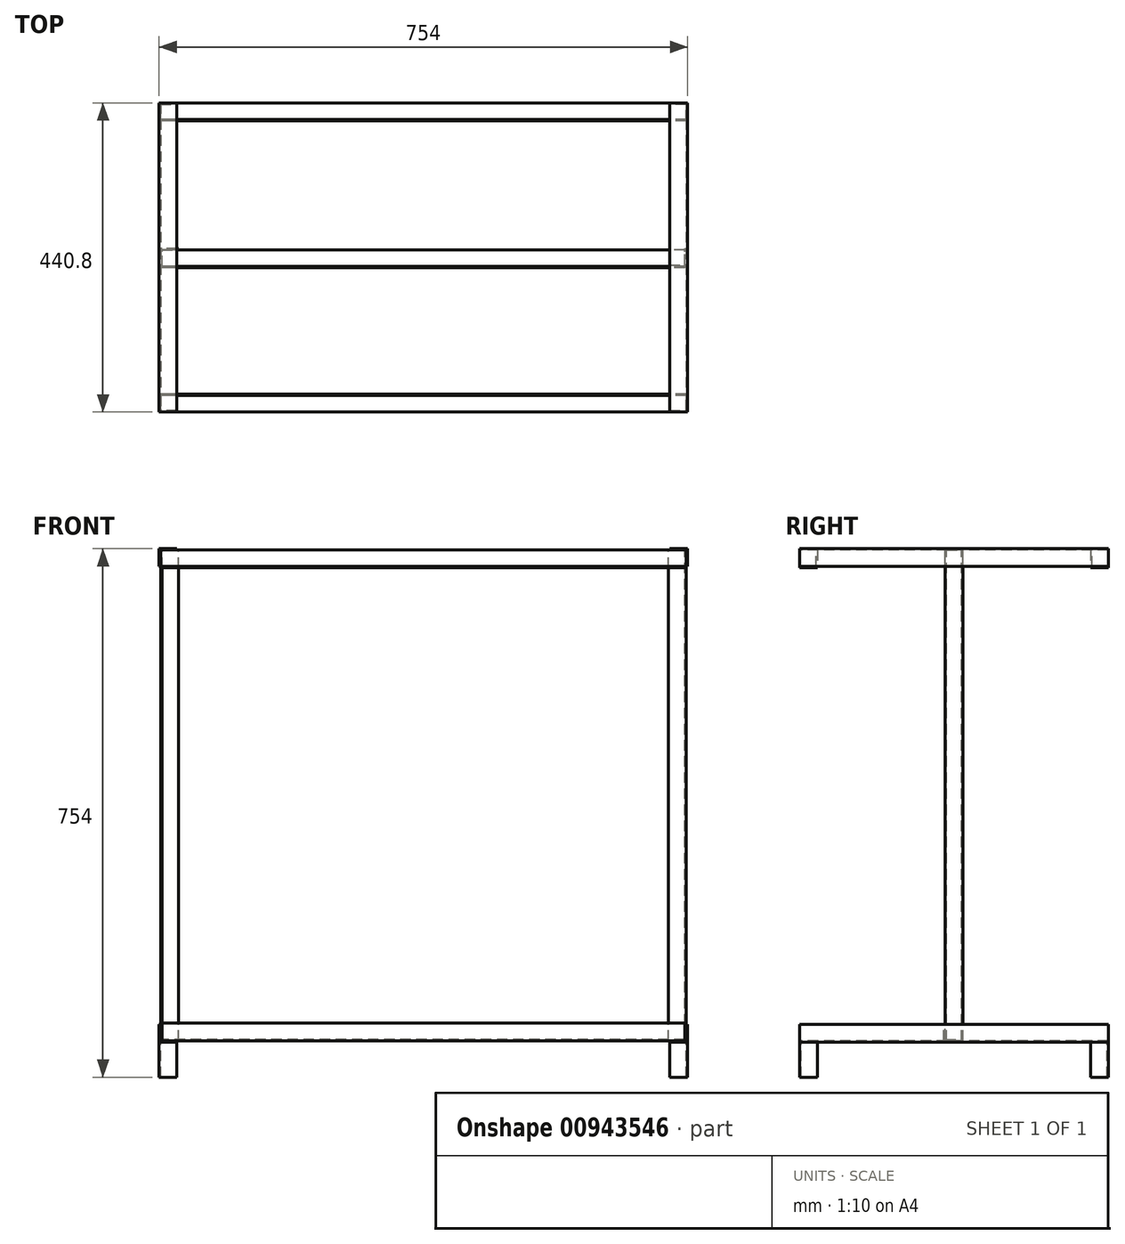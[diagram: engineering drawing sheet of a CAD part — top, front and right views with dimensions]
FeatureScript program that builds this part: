
annotation { "Feature Type Name" : "Feature", "Feature Type Description" : "" }
export const myFeature = defineFeature(function(context is Context, id is Id, definition is map)
    precondition{}
    {
        {
            var Q0;
            Q0=qCreatedBy(makeId("Front.planeOp"),FACE);
            var sketch = newSketch(context, id + "F0", { "sketchPlane" : qUnion([Q0])});
            skLineSegment(sketch, "E0.bottom", {"start": v(0, 0) * mm, "end": v(2, 0) * mm});
            skLineSegment(sketch, "E0.top", {"start": v(0, 25.4) * mm, "end": v(25.4, 25.4) * mm});
            skLineSegment(sketch, "E0.left", {"start": v(0, 0) * mm, "end": v(0, 25.4) * mm});
            skLineSegment(sketch, "E0.right", {"start": v(25.4, 23.4) * mm, "end": v(25.4, 25.4) * mm});
            skLineSegment(sketch, "E1.top", {"start": v(25.4, 23.4) * mm, "end": v(2, 23.4) * mm});
            skLineSegment(sketch, "E1.right", {"start": v(2, 0) * mm, "end": v(2, 23.4) * mm});
            skSolve(sketch);
        }
        {
            var Q0;
            Q0 = qSketchRegion(id + "F0", true);
            extrude(context, id + "F1", {"entities" : qUnion([Q0]), "oppositeDirection" : true, "depth" : 440.8 * mm, "offsetDistance" : 25 * mm});
        }
        {
            var Q0;
            Q0=makeQuery(id+"F1.opExtrude","SWEPT_FACE",FACE,{"disambiguationData":[OSD([sQuery(id+"F0.wireOp",EDGE,"E1.right")])]});
            var sketch = newSketch(context, id + "F2", { "sketchPlane" : qUnion([Q0])});
            skLineSegment(sketch, "E2", {"start": v(25.4, 23.4) * mm, "end": v(25.4, -2) * mm});
            skLineSegment(sketch, "E3", {"start": v(25.4, -2) * mm, "end": v(0, -2) * mm});
            skLineSegment(sketch, "E4", {"start": v(0, -2) * mm, "end": v(0, 0) * mm});
            skLineSegment(sketch, "E5", {"start": v(0, 0) * mm, "end": v(23.4, 0) * mm});
            skLineSegment(sketch, "E6", {"start": v(23.4, 0) * mm, "end": v(23.4, 23.4) * mm});
            skLineSegment(sketch, "E7", {"start": v(23.4, 23.4) * mm, "end": v(25.4, 23.4) * mm});
            skLineSegment(sketch, "E8", {"start": v(220.4, 23.4) * mm, "end": v(220.4, 0) * mm, "construction": true});
            skLineSegment(sketch, "E9.MirrorCS", {"start": v(417.4, 23.4) * mm, "end": v(415.4, 23.4) * mm});
            skLineSegment(sketch, "E10.MirrorCS", {"start": v(440.8, -2) * mm, "end": v(440.8, 0) * mm});
            skLineSegment(sketch, "E11.MirrorCS", {"start": v(415.4, 23.4) * mm, "end": v(415.4, -2) * mm});
            skLineSegment(sketch, "E12.MirrorCS", {"start": v(415.4, -2) * mm, "end": v(440.8, -2) * mm});
            skLineSegment(sketch, "E13.MirrorCS", {"start": v(440.8, 0) * mm, "end": v(417.4, 0) * mm});
            skLineSegment(sketch, "E14.MirrorCS", {"start": v(417.4, 0) * mm, "end": v(417.4, 23.4) * mm});
            skSolve(sketch);
        }
        {
            var Q0;
            {var subQ5=sQuery(id+"F2.wireOp",EDGE,"E6");Q0=makeQuery(id+"F2.imprint","IMPRINT",FACE,{"disambiguationData":[TD([[makeQuery(id+"F2.imprint","IMPRINT",EDGE,{"derivedFrom":subQ5}),-1.0]])]});}
            var Q1;
            {var subQ1=sQuery(id+"F2.wireOp",EDGE,"E3");Q1=makeQuery(id+"F2.imprint","IMPRINT",FACE,{"disambiguationData":[TD([[makeQuery(id+"F2.imprint","IMPRINT",EDGE,{"derivedFrom":subQ1}),-1.0]])]});}
            var Q2;
            {var subQ0=sQuery(id+"F2.wireOp",EDGE,"E9.MirrorCS");Q2=makeQuery(id+"F2.imprint","IMPRINT",FACE,{"disambiguationData":[TD([[makeQuery(id+"F2.imprint","IMPRINT",EDGE,{"derivedFrom":subQ0}),1.0]])]});}
            var Q3;
            Q3=makeQuery(id+"F2.imprint","IMPRINT",FACE,{"disambiguationData":[TD([[makeQuery(id+"F2.imprint","IMPRINT",EDGE,{"derivedFrom":sQuery(id+"F2.wireOp",EDGE,"E10.MirrorCS")}),1.0]])]});
            extrude(context, id + "F3", {"entities" : qUnion([Q0, Q1, Q2, Q3]), "depth" : 750 * mm, "offsetDistance" : 25 * mm});
        }
        {
            var Q0;
            Q0=qCreatedBy(makeId("Front.planeOp"),FACE);
            var sketch = newSketch(context, id + "F4", { "sketchPlane" : qUnion([Q0])});
            skLineSegment(sketch, "E15.0", {"start": v(752, 23.4) * mm, "end": v(2, 23.4) * mm, "construction": true});
            skLineSegment(sketch, "E15.1", {"start": v(752, -2) * mm, "end": v(2, -2) * mm, "construction": true});
            skLineSegment(sketch, "E16", {"start": v(377, 23.4) * mm, "end": v(377, -2) * mm, "construction": true});
            skLineSegment(sketch, "E17.0", {"start": v(0, 0) * mm, "end": v(0, 25.4) * mm});
            skLineSegment(sketch, "E17.1", {"start": v(0, 0) * mm, "end": v(2, 0) * mm});
            skLineSegment(sketch, "E17.2", {"start": v(2, 0) * mm, "end": v(2, 23.4) * mm});
            skLineSegment(sketch, "E17.3", {"start": v(0, 25.4) * mm, "end": v(25.4, 25.4) * mm});
            skLineSegment(sketch, "E17.4", {"start": v(25.4, 23.4) * mm, "end": v(25.4, 25.4) * mm});
            skLineSegment(sketch, "E18.MirrorCS", {"start": v(754, 0) * mm, "end": v(752, 0) * mm});
            skLineSegment(sketch, "E19.MirrorCS", {"start": v(728.6, 23.4) * mm, "end": v(728.6, 25.4) * mm});
            skLineSegment(sketch, "E20.MirrorCS", {"start": v(754, 0) * mm, "end": v(754, 25.4) * mm});
            skLineSegment(sketch, "E21.MirrorCS", {"start": v(754, 25.4) * mm, "end": v(728.6, 25.4) * mm});
            skLineSegment(sketch, "E22.MirrorCS", {"start": v(752, 0) * mm, "end": v(752, 23.4) * mm});
            skLineSegment(sketch, "E23", {"start": v(728.6, 23.4) * mm, "end": v(752, 23.4) * mm});
            skSolve(sketch);
        }
        {
            var Q0;
            Q0 = qSketchRegion(id + "F4", true);
            extrude(context, id + "F5", {"entities" : qUnion([Q0]), "oppositeDirection" : true, "depth" : 440.8 * mm, "offsetDistance" : 25 * mm});
        }
        {
            var Q0;
            Q0=makeQuery(id+"F1.opExtrude","SWEPT_FACE",FACE,{"disambiguationData":[OSD([sQuery(id+"F0.wireOp",EDGE,"E1.top")])]});
            var sketch = newSketch(context, id + "F6", { "sketchPlane" : qUnion([Q0])});
            skLineSegment(sketch, "E24.0", {"start": v(0, -440.8) * mm, "end": v(0, 0) * mm, "construction": true});
            skLineSegment(sketch, "E24.1", {"start": v(754, -440.8) * mm, "end": v(754, 0) * mm, "construction": true});
            skLineSegment(sketch, "E25", {"start": v(0, -220.4) * mm, "end": v(754, -220.4) * mm, "construction": true});
            skLineSegment(sketch, "E26", {"start": v(2, -220.4) * mm, "end": v(2, -207.7) * mm});
            skLineSegment(sketch, "E27", {"start": v(2, -207.7) * mm, "end": v(4, -207.7) * mm});
            skLineSegment(sketch, "E28", {"start": v(4, -207.7) * mm, "end": v(4, -231.1) * mm});
            skLineSegment(sketch, "E29", {"start": v(4, -231.1) * mm, "end": v(27.4, -231.1) * mm});
            skLineSegment(sketch, "E30", {"start": v(27.4, -231.1) * mm, "end": v(27.4, -233.1) * mm});
            skLineSegment(sketch, "E31", {"start": v(27.4, -233.1) * mm, "end": v(2, -233.1) * mm});
            skLineSegment(sketch, "E32", {"start": v(2, -233.1) * mm, "end": v(2, -220.4) * mm});
            skLineSegment(sketch, "E33", {"start": v(752, -220.4) * mm, "end": v(752, -207.7) * mm});
            skLineSegment(sketch, "E34", {"start": v(752, -207.7) * mm, "end": v(726.6, -207.7) * mm});
            skLineSegment(sketch, "E35", {"start": v(726.6, -207.7) * mm, "end": v(726.6, -209.7) * mm});
            skLineSegment(sketch, "E36", {"start": v(726.6, -209.7) * mm, "end": v(750, -209.7) * mm});
            skLineSegment(sketch, "E37", {"start": v(750, -209.7) * mm, "end": v(750, -233.1) * mm});
            skLineSegment(sketch, "E38", {"start": v(750, -233.1) * mm, "end": v(752, -233.1) * mm});
            skLineSegment(sketch, "E39", {"start": v(752, -233.1) * mm, "end": v(752, -220.4) * mm});
            skSolve(sketch);
        }
        {
            var Q0;
            Q0 = qSketchRegion(id + "F6", true);
            extrude(context, id + "F7", {"entities" : qUnion([Q0]), "depth" : 700 * mm, "offsetDistance" : 25 * mm});
        }
        {
            var Q0;
            Q0=qCreatedBy(makeId("Front.planeOp"),FACE);
            var sketch = newSketch(context, id + "F8", { "sketchPlane" : qUnion([Q0])});
            skLineSegment(sketch, "E40.0", {"start": v(27.4, -676.6) * mm, "end": v(27.4, 23.4) * mm, "construction": true});
            skLineSegment(sketch, "E40.1", {"start": v(726.6, -676.6) * mm, "end": v(726.6, 23.4) * mm, "construction": true});
            skLineSegment(sketch, "E41", {"start": v(27.4, -326.6) * mm, "end": v(726.6, -326.6) * mm, "construction": true});
            skLineSegment(sketch, "E42.0", {"start": v(0, 25.4) * mm, "end": v(25.4, 25.4) * mm, "construction": true});
            skLineSegment(sketch, "E42.1", {"start": v(2, 0) * mm, "end": v(2, 23.4) * mm, "construction": true});
            skLineSegment(sketch, "E42.2", {"start": v(25.4, 23.4) * mm, "end": v(2, 23.4) * mm, "construction": true});
            skLineSegment(sketch, "E42.3", {"start": v(25.4, 23.4) * mm, "end": v(25.4, 25.4) * mm, "construction": true});
            skLineSegment(sketch, "E42.4", {"start": v(0, 0) * mm, "end": v(0, 25.4) * mm, "construction": true});
            skLineSegment(sketch, "E42.5", {"start": v(0, 0) * mm, "end": v(2, 0) * mm, "construction": true});
            skLineSegment(sketch, "E42.6", {"start": v(754, 25.4) * mm, "end": v(728.6, 25.4) * mm, "construction": true});
            skLineSegment(sketch, "E42.7", {"start": v(728.6, 23.4) * mm, "end": v(752, 23.4) * mm, "construction": true});
            skLineSegment(sketch, "E42.8", {"start": v(728.6, 23.4) * mm, "end": v(728.6, 25.4) * mm, "construction": true});
            skLineSegment(sketch, "E42.9", {"start": v(754, 0) * mm, "end": v(754, 25.4) * mm, "construction": true});
            skLineSegment(sketch, "E42.10", {"start": v(752, 0) * mm, "end": v(752, 23.4) * mm, "construction": true});
            skLineSegment(sketch, "E42.11", {"start": v(754, 0) * mm, "end": v(752, 0) * mm, "construction": true});
            skLineSegment(sketch, "E43.MirrorCS", {"start": v(25.4, -676.6) * mm, "end": v(25.4, -678.6) * mm});
            skLineSegment(sketch, "E44.MirrorCS", {"start": v(0, -653.2) * mm, "end": v(2, -653.2) * mm});
            skLineSegment(sketch, "E45.MirrorCS", {"start": v(0, -653.2) * mm, "end": v(0, -678.6) * mm});
            skLineSegment(sketch, "E46.MirrorCS", {"start": v(25.4, -676.6) * mm, "end": v(2, -676.6) * mm});
            skLineSegment(sketch, "E47.MirrorCS", {"start": v(2, -653.2) * mm, "end": v(2, -676.6) * mm});
            skLineSegment(sketch, "E48.MirrorCS", {"start": v(0, -678.6) * mm, "end": v(25.4, -678.6) * mm});
            skLineSegment(sketch, "E49.MirrorCS", {"start": v(728.6, -676.6) * mm, "end": v(728.6, -678.6) * mm});
            skLineSegment(sketch, "E50.MirrorCS", {"start": v(754, -653.2) * mm, "end": v(752, -653.2) * mm});
            skLineSegment(sketch, "E51.MirrorCS", {"start": v(752, -653.2) * mm, "end": v(752, -676.6) * mm});
            skLineSegment(sketch, "E52.MirrorCS", {"start": v(754, -678.6) * mm, "end": v(728.6, -678.6) * mm});
            skLineSegment(sketch, "E53.MirrorCS", {"start": v(754, -653.2) * mm, "end": v(754, -678.6) * mm});
            skLineSegment(sketch, "E54.MirrorCS", {"start": v(728.6, -676.6) * mm, "end": v(752, -676.6) * mm});
            skSolve(sketch);
        }
        {
            var Q0;
            Q0 = qSketchRegion(id + "F8", true);
            extrude(context, id + "F9", {"entities" : qUnion([Q0]), "oppositeDirection" : true, "depth" : 440.8 * mm, "offsetDistance" : 25 * mm});
        }
        {
            var Q0;
            Q0=makeQuery(id+"F9.opExtrude","SWEPT_FACE",FACE,{"disambiguationData":[OSD([sQuery(id+"F8.wireOp",EDGE,"E48.MirrorCS")])]});
            var sketch = newSketch(context, id + "F10", { "sketchPlane" : qUnion([Q0])});
            skLineSegment(sketch, "E55", {"start": v(0, 0) * mm, "end": v(25.4, 0) * mm});
            skLineSegment(sketch, "E56", {"start": v(25.4, 0) * mm, "end": v(25.4, -2) * mm});
            skLineSegment(sketch, "E57", {"start": v(25.4, -2) * mm, "end": v(2, -2) * mm});
            skLineSegment(sketch, "E58", {"start": v(2, -2) * mm, "end": v(2, -25.4) * mm});
            skLineSegment(sketch, "E59", {"start": v(2, -25.4) * mm, "end": v(0, -25.4) * mm});
            skLineSegment(sketch, "E60", {"start": v(0, -25.4) * mm, "end": v(0, 0) * mm});
            skLineSegment(sketch, "E61", {"start": v(0, -440.8) * mm, "end": v(0, -415.4) * mm});
            skLineSegment(sketch, "E62", {"start": v(0, -415.4) * mm, "end": v(2, -415.4) * mm});
            skLineSegment(sketch, "E63", {"start": v(2, -415.4) * mm, "end": v(2, -438.8) * mm});
            skLineSegment(sketch, "E64", {"start": v(2, -438.8) * mm, "end": v(25.4, -438.8) * mm});
            skLineSegment(sketch, "E65", {"start": v(25.4, -438.8) * mm, "end": v(25.4, -440.8) * mm});
            skLineSegment(sketch, "E66", {"start": v(25.4, -440.8) * mm, "end": v(0, -440.8) * mm});
            skLineSegment(sketch, "E67.0", {"start": v(752, 0) * mm, "end": v(2, 0) * mm, "construction": true});
            skLineSegment(sketch, "E67.1", {"start": v(752, -440.8) * mm, "end": v(2, -440.8) * mm, "construction": true});
            skLineSegment(sketch, "E68", {"start": v(377, 0) * mm, "end": v(377, -440.8) * mm, "construction": true});
            skLineSegment(sketch, "E69.MirrorCS", {"start": v(728.6, -2) * mm, "end": v(752, -2) * mm});
            skLineSegment(sketch, "E70.MirrorCS", {"start": v(728.6, 0) * mm, "end": v(728.6, -2) * mm});
            skLineSegment(sketch, "E71.MirrorCS", {"start": v(754, 0) * mm, "end": v(728.6, 0) * mm});
            skLineSegment(sketch, "E72.MirrorCS", {"start": v(752, -2) * mm, "end": v(752, -25.4) * mm});
            skLineSegment(sketch, "E73.MirrorCS", {"start": v(754, -25.4) * mm, "end": v(754, 0) * mm});
            skLineSegment(sketch, "E74.MirrorCS", {"start": v(752, -25.4) * mm, "end": v(754, -25.4) * mm});
            skLineSegment(sketch, "E75.MirrorCS", {"start": v(728.6, -438.8) * mm, "end": v(728.6, -440.8) * mm});
            skLineSegment(sketch, "E76.MirrorCS", {"start": v(754, -415.4) * mm, "end": v(752, -415.4) * mm});
            skLineSegment(sketch, "E77.MirrorCS", {"start": v(752, -438.8) * mm, "end": v(728.6, -438.8) * mm});
            skLineSegment(sketch, "E78.MirrorCS", {"start": v(728.6, -440.8) * mm, "end": v(754, -440.8) * mm});
            skLineSegment(sketch, "E79.MirrorCS", {"start": v(752, -415.4) * mm, "end": v(752, -438.8) * mm});
            skLineSegment(sketch, "E80.MirrorCS", {"start": v(754, -440.8) * mm, "end": v(754, -415.4) * mm});
            skSolve(sketch);
        }
        {
            var Q0;
            Q0 = qSketchRegion(id + "F10", true);
            extrude(context, id + "F11", {"entities" : qUnion([Q0]), "depth" : 50 * mm, "offsetDistance" : 25 * mm});
        }
        {
            var Q0;
            Q0=makeQuery(id+"F7.opExtrude","SWEPT_FACE",FACE,{"disambiguationData":[OSD([sQuery(id+"F6.wireOp",EDGE,"E28")])]});
            var sketch = newSketch(context, id + "F12", { "sketchPlane" : qUnion([Q0])});
            skLineSegment(sketch, "E81", {"start": v(231.1, -676.6) * mm, "end": v(205.7, -676.6) * mm});
            skLineSegment(sketch, "E82", {"start": v(205.7, -676.6) * mm, "end": v(205.7, -651.2) * mm});
            skLineSegment(sketch, "E83", {"start": v(205.7, -651.2) * mm, "end": v(207.7, -651.2) * mm});
            skLineSegment(sketch, "E84", {"start": v(207.7, -651.2) * mm, "end": v(207.7, -674.6) * mm});
            skLineSegment(sketch, "E85", {"start": v(207.7, -674.6) * mm, "end": v(231.1, -674.6) * mm});
            skLineSegment(sketch, "E86", {"start": v(231.1, -674.6) * mm, "end": v(231.1, -676.6) * mm});
            skSolve(sketch);
        }
        {
            var Q0;
            Q0 = qSketchRegion(id + "F12", true);
            var Q1;
            Q1=makeQuery(id+"F7.opExtrude","SWEPT_FACE",FACE,{"disambiguationData":[OSD([sQuery(id+"F6.wireOp",EDGE,"E37")])]});
            extrude(context, id + "F13", {"entities" : qUnion([Q0]), "endBound" : BoundingType.UP_TO_SURFACE, "depth" : 25 * mm, "endBoundEntityFace" : qUnion([Q1]), "offsetDistance" : 25 * mm});
        }
    });
